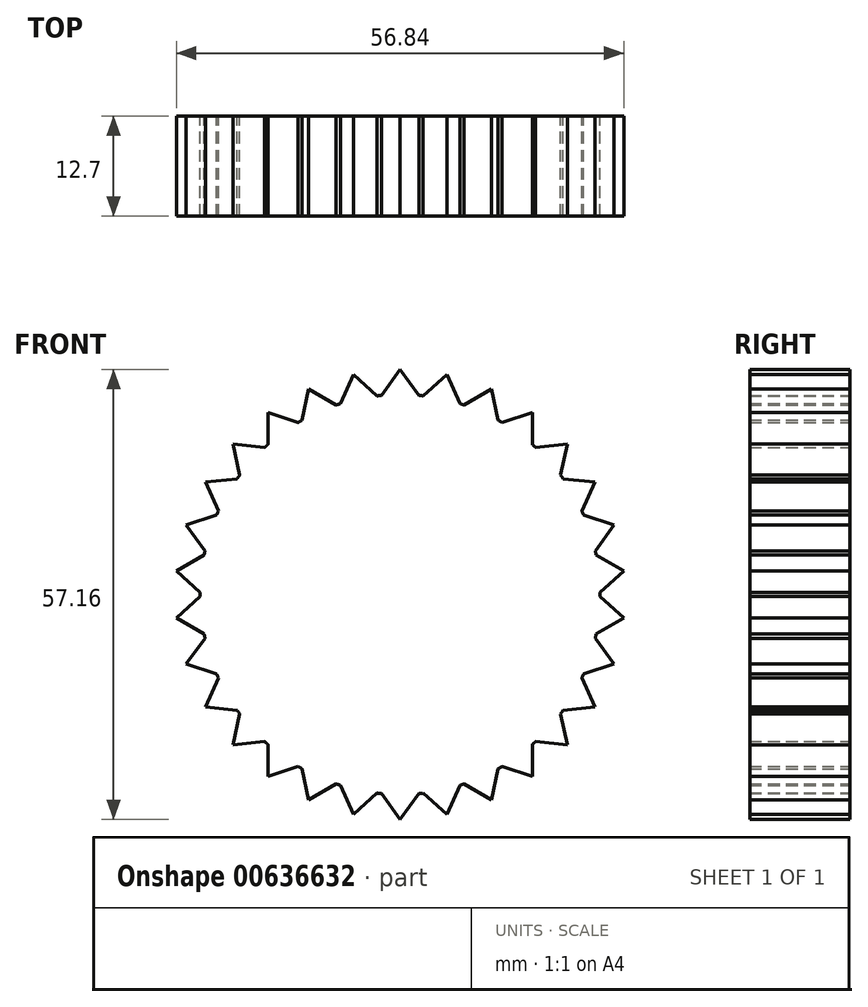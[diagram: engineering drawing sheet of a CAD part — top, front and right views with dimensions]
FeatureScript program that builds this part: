
annotation { "Feature Type Name" : "Feature", "Feature Type Description" : "" }
export const myFeature = defineFeature(function(context is Context, id is Id, definition is map)
    precondition{}
    {
        {
            var Q0;
            Q0=qCreatedBy(makeId("Front.planeOp"),FACE);
            var sketch = newSketch(context, id + "F0", { "sketchPlane" : qUnion([Q0])});
            skCircle(sketch, "E0", {"center": v(0, 0) * mm, "radius": 25.4 * mm});
            skLineSegment(sketch, "E1", {"start": v(0, 28.58) * mm, "end": v(0, 25.4) * mm, "construction": true});
            skLineSegment(sketch, "E2", {"start": v(0, 28.58) * mm, "end": v(-2.38, 25.29) * mm});
            skLineSegment(sketch, "E3.MirrorCS", {"start": v(0, 28.58) * mm, "end": v(2.38, 25.29) * mm});
            skLineSegment(sketch, "E4.1.0", {"start": v(-5.94, 27.95) * mm, "end": v(-7.58, 24.24) * mm});
            skLineSegment(sketch, "E4.1.1", {"start": v(-5.94, 27.95) * mm, "end": v(-2.93, 25.23) * mm});
            skLineSegment(sketch, "E4.2.0", {"start": v(-11.62, 26.1) * mm, "end": v(-12.46, 22.14) * mm});
            skLineSegment(sketch, "E4.2.1", {"start": v(-11.62, 26.1) * mm, "end": v(-8.12, 24.07) * mm});
            skLineSegment(sketch, "E4.3.0", {"start": v(-16.8, 23.12) * mm, "end": v(-16.79, 19.06) * mm});
            skLineSegment(sketch, "E4.3.1", {"start": v(-16.8, 23.12) * mm, "end": v(-12.94, 21.86) * mm});
            skLineSegment(sketch, "E4.4.0", {"start": v(-21.24, 19.12) * mm, "end": v(-20.38, 15.16) * mm});
            skLineSegment(sketch, "E4.4.1", {"start": v(-21.24, 19.12) * mm, "end": v(-17.2, 18.69) * mm});
            skLineSegment(sketch, "E4.5.0", {"start": v(-24.75, 14.29) * mm, "end": v(-23.09, 10.59) * mm});
            skLineSegment(sketch, "E4.5.1", {"start": v(-24.75, 14.29) * mm, "end": v(-20.71, 14.7) * mm});
            skLineSegment(sketch, "E4.6.0", {"start": v(-27.18, 8.83) * mm, "end": v(-24.79, 5.56) * mm});
            skLineSegment(sketch, "E4.6.1", {"start": v(-27.18, 8.83) * mm, "end": v(-23.32, 10.07) * mm});
            skLineSegment(sketch, "E4.7.0", {"start": v(-28.42, 2.99) * mm, "end": v(-25.4, 0.28) * mm});
            skLineSegment(sketch, "E4.7.1", {"start": v(-28.42, 2.99) * mm, "end": v(-24.9, 5) * mm});
            skLineSegment(sketch, "E4.8.0", {"start": v(-28.42, -2.99) * mm, "end": v(-24.9, -5) * mm});
            skLineSegment(sketch, "E4.8.1", {"start": v(-28.42, -2.99) * mm, "end": v(-25.4, -0.28) * mm});
            skLineSegment(sketch, "E4.9.0", {"start": v(-27.18, -8.83) * mm, "end": v(-23.32, -10.07) * mm});
            skLineSegment(sketch, "E4.9.1", {"start": v(-27.18, -8.83) * mm, "end": v(-24.79, -5.56) * mm});
            skLineSegment(sketch, "E4.10.0", {"start": v(-24.75, -14.29) * mm, "end": v(-20.71, -14.7) * mm});
            skLineSegment(sketch, "E4.10.1", {"start": v(-24.75, -14.29) * mm, "end": v(-23.09, -10.59) * mm});
            skLineSegment(sketch, "E4.11.0", {"start": v(-21.24, -19.12) * mm, "end": v(-17.2, -18.69) * mm});
            skLineSegment(sketch, "E4.11.1", {"start": v(-21.24, -19.12) * mm, "end": v(-20.38, -15.16) * mm});
            skLineSegment(sketch, "E4.12.0", {"start": v(-16.8, -23.12) * mm, "end": v(-12.94, -21.86) * mm});
            skLineSegment(sketch, "E4.12.1", {"start": v(-16.8, -23.12) * mm, "end": v(-16.79, -19.06) * mm});
            skLineSegment(sketch, "E4.13.0", {"start": v(-11.62, -26.1) * mm, "end": v(-8.12, -24.07) * mm});
            skLineSegment(sketch, "E4.13.1", {"start": v(-11.62, -26.1) * mm, "end": v(-12.46, -22.14) * mm});
            skLineSegment(sketch, "E4.14.0", {"start": v(-5.94, -27.95) * mm, "end": v(-2.93, -25.23) * mm});
            skLineSegment(sketch, "E4.14.1", {"start": v(-5.94, -27.95) * mm, "end": v(-7.58, -24.24) * mm});
            skLineSegment(sketch, "E4.15.0", {"start": v(0, -28.58) * mm, "end": v(2.38, -25.29) * mm});
            skLineSegment(sketch, "E4.15.1", {"start": v(0, -28.58) * mm, "end": v(-2.38, -25.29) * mm});
            skLineSegment(sketch, "E4.16.0", {"start": v(5.94, -27.95) * mm, "end": v(7.58, -24.24) * mm});
            skLineSegment(sketch, "E4.16.1", {"start": v(5.94, -27.95) * mm, "end": v(2.93, -25.23) * mm});
            skLineSegment(sketch, "E4.17.0", {"start": v(11.62, -26.1) * mm, "end": v(12.46, -22.14) * mm});
            skLineSegment(sketch, "E4.17.1", {"start": v(11.62, -26.1) * mm, "end": v(8.12, -24.07) * mm});
            skLineSegment(sketch, "E4.18.0", {"start": v(16.8, -23.12) * mm, "end": v(16.79, -19.06) * mm});
            skLineSegment(sketch, "E4.18.1", {"start": v(16.8, -23.12) * mm, "end": v(12.94, -21.86) * mm});
            skLineSegment(sketch, "E4.19.0", {"start": v(21.24, -19.12) * mm, "end": v(20.38, -15.16) * mm});
            skLineSegment(sketch, "E4.19.1", {"start": v(21.24, -19.12) * mm, "end": v(17.2, -18.69) * mm});
            skLineSegment(sketch, "E4.20.0", {"start": v(24.75, -14.29) * mm, "end": v(23.09, -10.59) * mm});
            skLineSegment(sketch, "E4.20.1", {"start": v(24.75, -14.29) * mm, "end": v(20.71, -14.7) * mm});
            skLineSegment(sketch, "E4.21.0", {"start": v(27.18, -8.83) * mm, "end": v(24.79, -5.56) * mm});
            skLineSegment(sketch, "E4.21.1", {"start": v(27.18, -8.83) * mm, "end": v(23.32, -10.07) * mm});
            skLineSegment(sketch, "E4.22.0", {"start": v(28.42, -2.99) * mm, "end": v(25.4, -0.28) * mm});
            skLineSegment(sketch, "E4.22.1", {"start": v(28.42, -2.99) * mm, "end": v(24.9, -5) * mm});
            skLineSegment(sketch, "E4.23.0", {"start": v(28.42, 2.99) * mm, "end": v(24.9, 5) * mm});
            skLineSegment(sketch, "E4.23.1", {"start": v(28.42, 2.99) * mm, "end": v(25.4, 0.28) * mm});
            skLineSegment(sketch, "E4.24.0", {"start": v(27.18, 8.83) * mm, "end": v(23.32, 10.07) * mm});
            skLineSegment(sketch, "E4.24.1", {"start": v(27.18, 8.83) * mm, "end": v(24.79, 5.56) * mm});
            skLineSegment(sketch, "E4.25.0", {"start": v(24.75, 14.29) * mm, "end": v(20.71, 14.7) * mm});
            skLineSegment(sketch, "E4.25.1", {"start": v(24.75, 14.29) * mm, "end": v(23.09, 10.59) * mm});
            skLineSegment(sketch, "E4.26.0", {"start": v(21.24, 19.12) * mm, "end": v(17.2, 18.69) * mm});
            skLineSegment(sketch, "E4.26.1", {"start": v(21.24, 19.12) * mm, "end": v(20.38, 15.16) * mm});
            skLineSegment(sketch, "E4.27.0", {"start": v(16.8, 23.12) * mm, "end": v(12.94, 21.86) * mm});
            skLineSegment(sketch, "E4.27.1", {"start": v(16.8, 23.12) * mm, "end": v(16.79, 19.06) * mm});
            skLineSegment(sketch, "E4.28.0", {"start": v(11.62, 26.1) * mm, "end": v(8.12, 24.07) * mm});
            skLineSegment(sketch, "E4.28.1", {"start": v(11.62, 26.1) * mm, "end": v(12.46, 22.14) * mm});
            skLineSegment(sketch, "E4.29.0", {"start": v(5.94, 27.95) * mm, "end": v(2.93, 25.23) * mm});
            skLineSegment(sketch, "E4.29.1", {"start": v(5.94, 27.95) * mm, "end": v(7.58, 24.24) * mm});
            skSolve(sketch);
        }
        {
            var Q0;
            Q0 = qSketchRegion(id + "F0", true);
            extrude(context, id + "F1", {"entities" : qUnion([Q0]), "depth" : 12.7 * mm, "offsetDistance" : 25.4 * mm});
        }
    });
